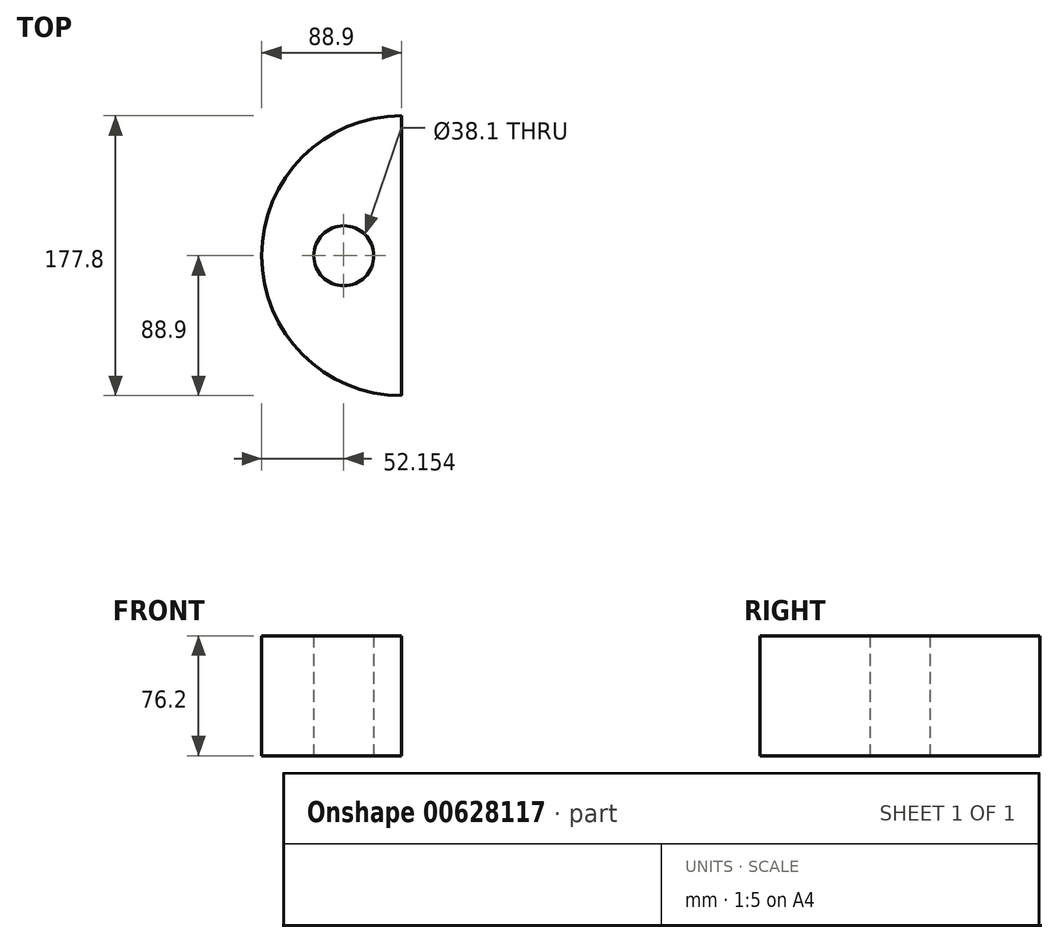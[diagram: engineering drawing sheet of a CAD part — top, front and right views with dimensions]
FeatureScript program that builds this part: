
annotation { "Feature Type Name" : "Feature", "Feature Type Description" : "" }
export const myFeature = defineFeature(function(context is Context, id is Id, definition is map)
    precondition{}
    {
        {
            var Q0;
            Q0=qCreatedBy(makeId("Top.planeOp"),FACE);
            var sketch = newSketch(context, id + "F0", { "sketchPlane" : qUnion([Q0])});
            skArc(sketch, "E0", {"start": v(0, 88.9) * mm, "mid": v(-88.9, 0) * mm, "end": v(0, -88.9) * mm});
            skLineSegment(sketch, "E1", {"start": v(0, 88.9) * mm, "end": v(0, -88.9) * mm});
            skCircle(sketch, "E2", {"center": v(-36.75, 0) * mm, "radius": 19.05 * mm});
            skSolve(sketch);
        }
        {
            var Q0;
            Q0 = qSketchRegion(id + "F0", true);
            extrude(context, id + "F1", {"entities" : qUnion([Q0]), "depth" : 76.2 * mm, "offsetDistance" : 25.4 * mm});
        }
    });
